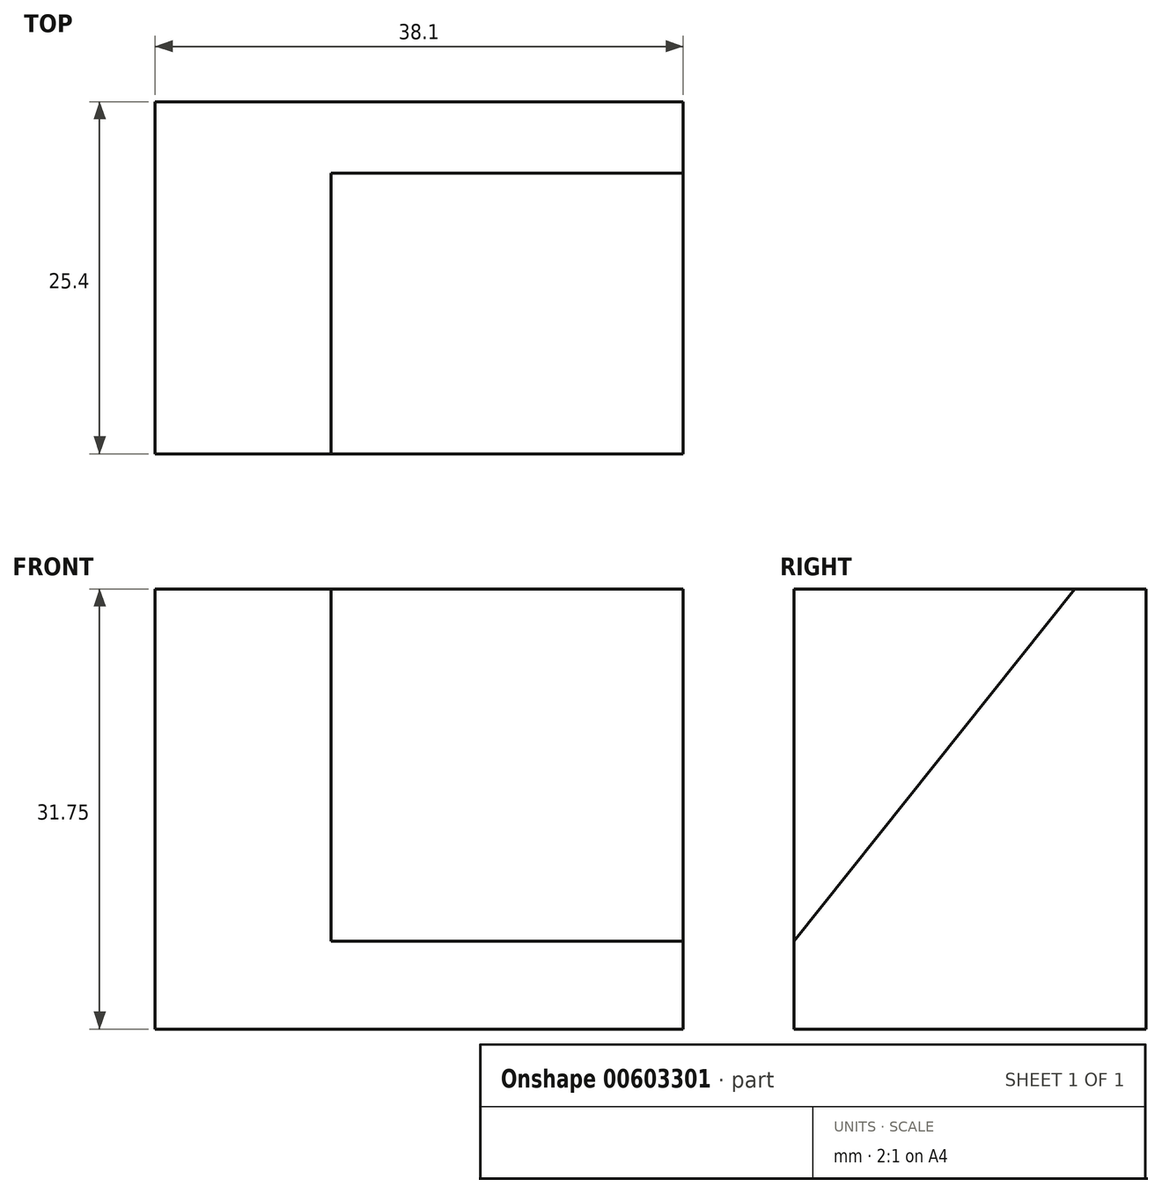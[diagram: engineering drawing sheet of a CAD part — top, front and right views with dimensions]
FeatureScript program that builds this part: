
annotation { "Feature Type Name" : "Feature", "Feature Type Description" : "" }
export const myFeature = defineFeature(function(context is Context, id is Id, definition is map)
    precondition{}
    {
        {
            var Q0;
            Q0=qCreatedBy(makeId("Right.planeOp"),FACE);
            var sketch = newSketch(context, id + "F0", { "sketchPlane" : qUnion([Q0])});
            skLineSegment(sketch, "E0", {"start": v(0, 0) * mm, "end": v(-25.4, 0) * mm});
            skLineSegment(sketch, "E1", {"start": v(-25.4, 0) * mm, "end": v(-25.4, 6.35) * mm});
            skLineSegment(sketch, "E2", {"start": v(0, 0) * mm, "end": v(0, 31.75) * mm});
            skLineSegment(sketch, "E3", {"start": v(0, 31.75) * mm, "end": v(-5.16, 31.75) * mm});
            skLineSegment(sketch, "E4", {"start": v(-5.16, 31.75) * mm, "end": v(-25.4, 6.35) * mm});
            skSolve(sketch);
        }
        {
            var Q0;
            Q0 = qSketchRegion(id + "F0", true);
            extrude(context, id + "F1", {"entities" : qUnion([Q0]), "depth" : 25.4 * mm, "offsetDistance" : 25.4 * mm});
        }
        {
            var Q0;
            Q0=qCreatedBy(makeId("Front.planeOp"),FACE);
            var sketch = newSketch(context, id + "F2", { "sketchPlane" : qUnion([Q0])});
            skLineSegment(sketch, "E5", {"start": v(0, 0) * mm, "end": v(-12.7, 0) * mm});
            skLineSegment(sketch, "E6", {"start": v(-12.7, 0) * mm, "end": v(-12.7, 31.75) * mm});
            skLineSegment(sketch, "E7", {"start": v(-12.7, 31.75) * mm, "end": v(0, 31.75) * mm});
            skLineSegment(sketch, "E8", {"start": v(0, 31.75) * mm, "end": v(0, 0) * mm});
            skSolve(sketch);
        }
        {
            var Q0;
            Q0 = qSketchRegion(id + "F2", true);
            extrude(context, id + "F3", {"entities" : qUnion([Q0]), "operationType" : NewBodyOperationType.ADD, "depth" : 25.4 * mm, "offsetDistance" : 25.4 * mm});
        }
    });
